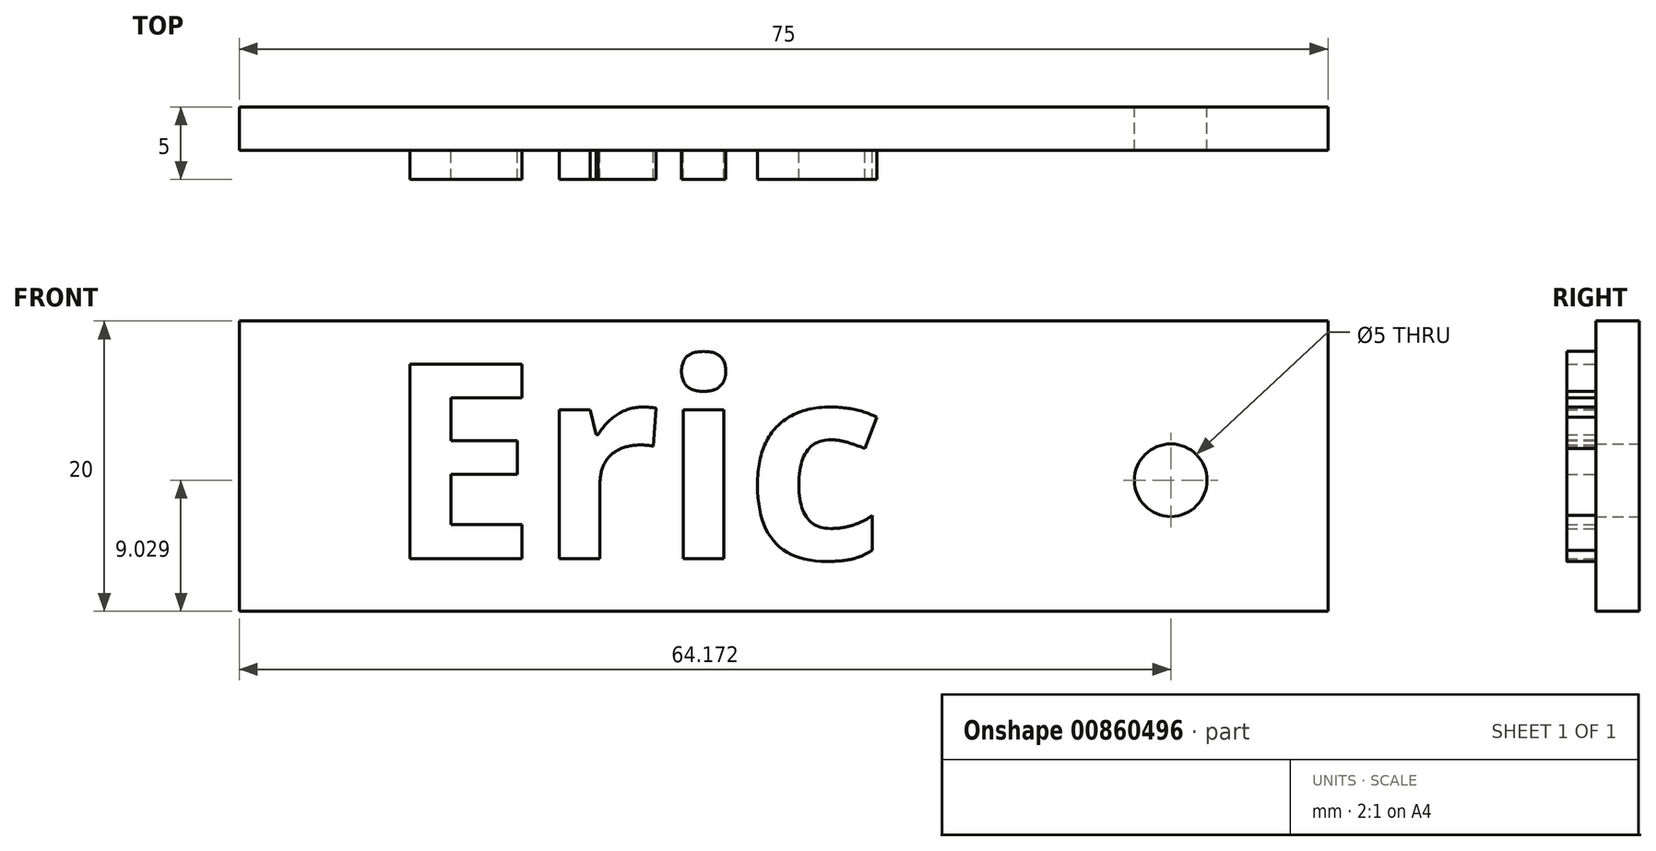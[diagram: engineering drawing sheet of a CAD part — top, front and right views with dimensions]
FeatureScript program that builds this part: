
annotation { "Feature Type Name" : "Feature", "Feature Type Description" : "" }
export const myFeature = defineFeature(function(context is Context, id is Id, definition is map)
    precondition{}
    {
        {
            var Q0;
            Q0=qCreatedBy(makeId("Front.planeOp"),FACE);
            var sketch = newSketch(context, id + "F0", { "sketchPlane" : qUnion([Q0])});
            skLineSegment(sketch, "E0.bottom", {"start": v(0, 0) * mm, "end": v(75, 0) * mm});
            skLineSegment(sketch, "E0.top", {"start": v(0, -20) * mm, "end": v(75, -20) * mm});
            skLineSegment(sketch, "E0.left", {"start": v(0, 0) * mm, "end": v(0, -20) * mm});
            skLineSegment(sketch, "E0.right", {"start": v(75, 0) * mm, "end": v(75, -20) * mm});
            skCircle(sketch, "E1", {"center": v(64.17, -10.97) * mm, "radius": 2.5 * mm});
            skSolve(sketch);
        }
        {
            var Q0;
            Q0 = qSketchRegion(id + "F0", true);
            extrude(context, id + "F1", {"entities" : qUnion([Q0]), "depth" : 3 * mm, "offsetDistance" : 25 * mm});
        }
        {
            var Q0;
            Q0=makeQuery(id+"F1.opExtrude","CAP_FACE",FACE,{"disambiguationData":[OSD([sQuery(id+"F0.wireOp",EDGE,"E0.bottom"),sQuery(id+"F0.wireOp",EDGE,"E0.top"),sQuery(id+"F0.wireOp",EDGE,"E0.left"),sQuery(id+"F0.wireOp",EDGE,"E0.right"),sQuery(id+"F0.wireOp",EDGE,"E1")])],"isStart":false});
            var sketch = newSketch(context, id + "F2", { "sketchPlane" : qUnion([Q0])});
            skText(sketch, "E2", { "text": "Eric", "fontName": "OpenSans-Bold.ttf"});
            const initialGuessF2  = {"E2": [0.01007, -0.01638, 1, 0, 0.01353]};
            skSetInitialGuess(sketch, initialGuessF2);
            skSolve(sketch);
        }
        {
            var Q0;
            Q0 = qSketchRegion(id + "F2", true);
            extrude(context, id + "F3", {"entities" : qUnion([Q0]), "operationType" : NewBodyOperationType.ADD, "depth" : 2 * mm, "offsetDistance" : 25 * mm});
        }
    });
